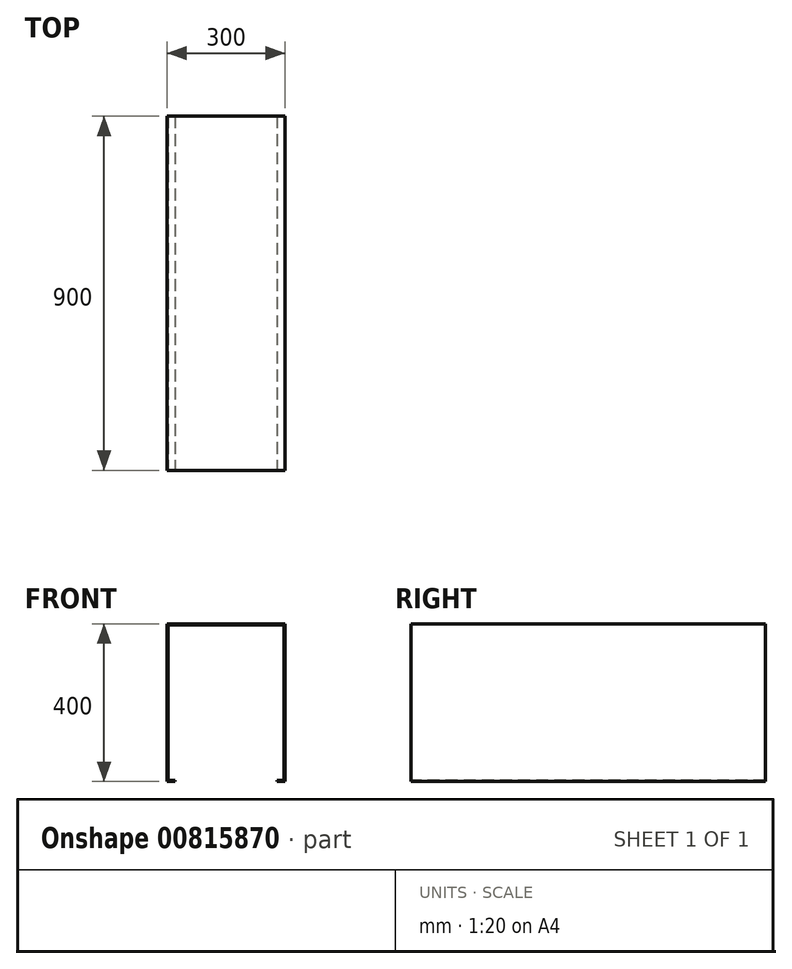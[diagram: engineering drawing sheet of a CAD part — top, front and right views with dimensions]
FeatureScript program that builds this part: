
annotation { "Feature Type Name" : "Feature", "Feature Type Description" : "" }
export const myFeature = defineFeature(function(context is Context, id is Id, definition is map)
    precondition{}
    {
        {
            var Q0;
            Q0=qCreatedBy(makeId("Front.planeOp"),FACE);
            var sketch = newSketch(context, id + "F0", { "sketchPlane" : qUnion([Q0])});
            skLineSegment(sketch, "E0", {"start": v(0, 0) * mm, "end": v(-20, 0) * mm});
            skLineSegment(sketch, "E1", {"start": v(-20, 0) * mm, "end": v(-20, 400) * mm});
            skLineSegment(sketch, "E2", {"start": v(-20, 400) * mm, "end": v(280, 400) * mm});
            skLineSegment(sketch, "E3", {"start": v(280, 400) * mm, "end": v(280, 0) * mm});
            skLineSegment(sketch, "E4", {"start": v(280, 0) * mm, "end": v(260, 0) * mm});
            skLineSegment(sketch, "E5.0", {"start": v(277, 3) * mm, "end": v(260, 3) * mm});
            skLineSegment(sketch, "E5.1", {"start": v(0, 3) * mm, "end": v(-17, 3) * mm});
            skLineSegment(sketch, "E5.2", {"start": v(-17, 3) * mm, "end": v(-17, 397) * mm});
            skLineSegment(sketch, "E5.3", {"start": v(-17, 397) * mm, "end": v(277, 397) * mm});
            skLineSegment(sketch, "E5.4", {"start": v(277, 397) * mm, "end": v(277, 3) * mm});
            skLineSegment(sketch, "E6", {"start": v(0, 3) * mm, "end": v(0, 0) * mm});
            skLineSegment(sketch, "E7", {"start": v(260, 3) * mm, "end": v(260, 0) * mm});
            skSolve(sketch);
        }
        {
            var Q0;
            Q0 = qSketchRegion(id + "F0", true);
            extrude(context, id + "F1", {"entities" : qUnion([Q0]), "oppositeDirection" : true, "depth" : 900 * mm, "offsetDistance" : 25 * mm});
        }
    });
